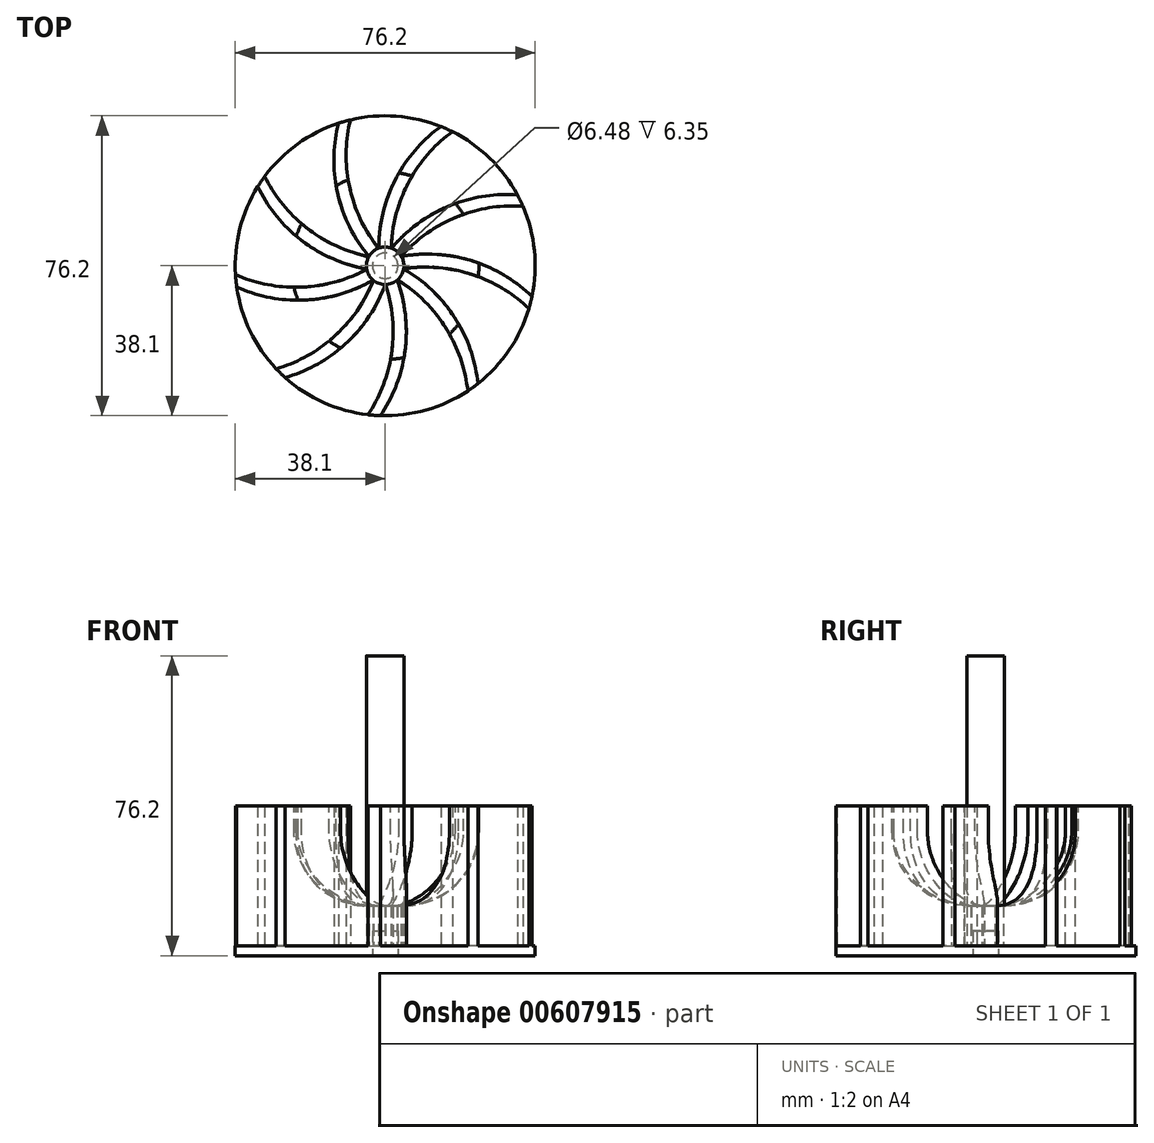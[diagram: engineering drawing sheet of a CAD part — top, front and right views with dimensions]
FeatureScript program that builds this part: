
annotation { "Feature Type Name" : "Feature", "Feature Type Description" : "" }
export const myFeature = defineFeature(function(context is Context, id is Id, definition is map)
    precondition{}
    {
        {
            var Q0;
            Q0=qCreatedBy(makeId("Top.planeOp"),FACE);
            var sketch = newSketch(context, id + "F0", { "sketchPlane" : qUnion([Q0])});
            skCircle(sketch, "E0", {"center": v(0, 0) * mm, "radius": 38.1 * mm});
            skSolve(sketch);
        }
        {
            var Q0;
            Q0=makeQuery(id+"F0.imprint","IMPRINT",FACE,{"disambiguationData":[TD([[makeQuery(id+"F0.imprint","IMPRINT",EDGE,{"derivedFrom":sQuery(id+"F0.wireOp",EDGE,"E0")}),1.0]])]});
            extrude(context, id + "F1", {"entities" : qUnion([Q0]), "depth" : 2.54 * mm, "offsetDistance" : 25.4 * mm});
        }
        {
            var Q0;
            Q0=makeQuery(id+"F1.opExtrude","CAP_FACE",FACE,{"disambiguationData":[OSD([sQuery(id+"F0.wireOp",EDGE,"E0")])],"isStart":false});
            var sketch = newSketch(context, id + "F2", { "sketchPlane" : qUnion([Q0])});
            skArc(sketch, "E1", {"start": v(0, -4.76) * mm, "mid": v(0.04, -4.76) * mm, "end": v(0.09, -4.76) * mm});
            skArc(sketch, "E2", {"start": v(-27.68, -26.18) * mm, "mid": v(-12.74, -17.8) * mm, "end": v(-3, -3.7) * mm});
            skArc(sketch, "E3", {"start": v(-25.4, -28.4) * mm, "mid": v(-9.85, -19.64) * mm, "end": v(0, -4.76) * mm});
            skLineSegment(sketch, "E4", {"start": v(-3, -3.7) * mm, "end": v(0, -4.76) * mm, "construction": true});
            skLineSegment(sketch, "E5", {"start": v(-27.68, -26.18) * mm, "end": v(-25.4, -28.4) * mm, "construction": true});
            skArc(sketch, "E6.1.0", {"start": v(-1.2, -38.08) * mm, "mid": v(5.08, -21.38) * mm, "end": v(3.06, -3.65) * mm});
            skArc(sketch, "E6.1.1", {"start": v(-4.37, -37.85) * mm, "mid": v(1.68, -21.82) * mm, "end": v(0.09, -4.76) * mm});
            skArc(sketch, "E6.2.0", {"start": v(23.56, -29.95) * mm, "mid": v(17.63, -13.11) * mm, "end": v(4.7, -0.83) * mm});
            skArc(sketch, "E6.2.1", {"start": v(20.98, -31.8) * mm, "mid": v(15.3, -15.64) * mm, "end": v(3.13, -3.6) * mm});
            skArc(sketch, "E6.3.0", {"start": v(37.3, -7.8) * mm, "mid": v(21.93, 1.29) * mm, "end": v(4.12, 2.38) * mm});
            skArc(sketch, "E6.3.1", {"start": v(36.51, -10.88) * mm, "mid": v(21.78, -2.14) * mm, "end": v(4.7, -0.74) * mm});
            skArc(sketch, "E6.4.0", {"start": v(33.58, 18) * mm, "mid": v(15.98, 15.08) * mm, "end": v(1.63, 4.48) * mm});
            skArc(sketch, "E6.4.1", {"start": v(34.96, 15.14) * mm, "mid": v(18.06, 12.36) * mm, "end": v(4.08, 2.46) * mm});
            skArc(sketch, "E6.5.0", {"start": v(14.16, 35.37) * mm, "mid": v(2.54, 21.83) * mm, "end": v(-1.63, 4.48) * mm});
            skArc(sketch, "E6.5.1", {"start": v(17.05, 34.07) * mm, "mid": v(5.89, 21.08) * mm, "end": v(1.55, 4.5) * mm});
            skArc(sketch, "E6.6.0", {"start": v(-11.9, 36.2) * mm, "mid": v(-12.08, 18.35) * mm, "end": v(-4.12, 2.38) * mm});
            skArc(sketch, "E6.6.1", {"start": v(-8.84, 37.06) * mm, "mid": v(-9.04, 19.93) * mm, "end": v(-1.71, 4.44) * mm});
            skArc(sketch, "E6.7.0", {"start": v(-32.38, 20.08) * mm, "mid": v(-21.05, 6.3) * mm, "end": v(-4.7, -0.83) * mm});
            skArc(sketch, "E6.7.1", {"start": v(-30.6, 22.7) * mm, "mid": v(-19.73, 9.46) * mm, "end": v(-4.17, 2.3) * mm});
            skArc(sketch, "E6.8.0", {"start": v(-37.71, -5.43) * mm, "mid": v(-20.17, -8.71) * mm, "end": v(-3.06, -3.65) * mm});
            skArc(sketch, "E6.8.1", {"start": v(-38.03, -2.27) * mm, "mid": v(-21.2, -5.44) * mm, "end": v(-4.67, -0.91) * mm});
            skArc(sketch, "E7.trimOffspring", {"start": v(-3.06, -3.65) * mm, "mid": v(-3.03, -3.68) * mm, "end": v(-3, -3.7) * mm});
            skArc(sketch, "E8.trimOffspring", {"start": v(-4.7, -0.83) * mm, "mid": v(-4.68, -0.87) * mm, "end": v(-4.67, -0.91) * mm});
            skArc(sketch, "E9.trimOffspring", {"start": v(3.06, -3.65) * mm, "mid": v(3.1, -3.62) * mm, "end": v(3.13, -3.6) * mm});
            skArc(sketch, "E10.trimOffspring", {"start": v(4.7, -0.83) * mm, "mid": v(4.7, -0.78) * mm, "end": v(4.7, -0.74) * mm});
            skArc(sketch, "E11.trimOffspring", {"start": v(4.12, 2.38) * mm, "mid": v(4.1, 2.42) * mm, "end": v(4.08, 2.46) * mm});
            skArc(sketch, "E12.trimOffspring", {"start": v(1.63, 4.48) * mm, "mid": v(1.59, 4.5) * mm, "end": v(1.55, 4.5) * mm});
            skArc(sketch, "E13.trimOffspring", {"start": v(-4.12, 2.38) * mm, "mid": v(-4.15, 2.34) * mm, "end": v(-4.17, 2.3) * mm});
            skArc(sketch, "E14.trimOffspring", {"start": v(-1.63, 4.48) * mm, "mid": v(-1.67, 4.46) * mm, "end": v(-1.71, 4.44) * mm});
            skCircle(sketch, "E15", {"center": v(0, 0) * mm, "radius": 38.1 * mm});
            skSolve(sketch);
        }
        {
            var Q0;
            Q0=makeQuery(id+"F2.imprint","IMPRINT",FACE,{"disambiguationData":[TD([[makeQuery(id+"F2.imprint","IMPRINT",EDGE,{"derivedFrom":sQuery(id+"F2.wireOp",EDGE,"E1")}),1.0]])]});
            extrude(context, id + "F3", {"entities" : qUnion([Q0]), "operationType" : NewBodyOperationType.ADD, "depth" : 35.56 * mm, "offsetDistance" : 25.4 * mm});
        }
        {
            var Q0;
            Q0=qCreatedBy(makeId("Front.planeOp"),FACE);
            var sketch = newSketch(context, id + "F4", { "sketchPlane" : qUnion([Q0])});
            skLineSegment(sketch, "E16", {"start": v(0, 0) * mm, "end": v(0, 35.7) * mm, "construction": true});
            skLineSegment(sketch, "E17", {"start": v(-4.76, 44.45) * mm, "end": v(-4.76, 12.7) * mm});
            skArc(sketch, "E18", {"start": v(-23.81, 31.75) * mm, "mid": v(-18.23, 18.28) * mm, "end": v(-4.76, 12.7) * mm});
            skLineSegment(sketch, "E19", {"start": v(-23.81, 31.75) * mm, "end": v(-23.81, 44.45) * mm});
            skLineSegment(sketch, "E20", {"start": v(-23.81, 44.45) * mm, "end": v(-4.76, 44.45) * mm});
            skSolve(sketch);
        }
        {
            var Q0;
            Q0=makeQuery(id+"F4.imprint","IMPRINT",FACE,{"disambiguationData":[TD([[makeQuery(id+"F4.imprint","IMPRINT",EDGE,{"derivedFrom":sQuery(id+"F4.wireOp",EDGE,"E17")}),-1.0]])]});
            var Q1;
            Q1=sQuery(id+"F4.wireOp",EDGE,"E16");
            revolve(context, id + "F5", {"operationType" : NewBodyOperationType.REMOVE, "entities" : qUnion([Q0]), "axis" : qUnion([Q1]), "revolveType" : RevolveType.FULL, "oppositeDirection" : true});
        }
        {
            var Q0;
            {var subQ0=sQuery(id+"F2.wireOp",EDGE,"E9.trimOffspring");var subQ1=sQuery(id+"F2.wireOp",EDGE,"E8.trimOffspring");var subQ2=sQuery(id+"F2.wireOp",EDGE,"E1");var subQ3=sQuery(id+"F2.wireOp",EDGE,"E7.trimOffspring");var subQ4=sQuery(id+"F2.wireOp",EDGE,"E10.trimOffspring");var subQ5=sQuery(id+"F2.wireOp",EDGE,"E11.trimOffspring");var subQ6=sQuery(id+"F2.wireOp",EDGE,"E12.trimOffspring");var subQ7=sQuery(id+"F2.wireOp",EDGE,"E13.trimOffspring");var subQ8=sQuery(id+"F2.wireOp",EDGE,"E14.trimOffspring");Q0=makeQuery(id+"F5.boolean.opBoolean","SPLIT",FACE,{"disambiguationData":[TD([makeQuery(id+"F3.opExtrude","SWEPT_FACE",FACE,{"disambiguationData":[OSD([subQ2])]})])],"derivedFrom":makeQuery(id+"F3.opExtrude","CAP_FACE",FACE,{"disambiguationData":[OSD([subQ2,sQuery(id+"F2.wireOp",EDGE,"E2"),sQuery(id+"F2.wireOp",EDGE,"E3"),sQuery(id+"F2.wireOp",EDGE,"E6.1.0"),sQuery(id+"F2.wireOp",EDGE,"E6.1.1"),sQuery(id+"F2.wireOp",EDGE,"E6.2.0"),sQuery(id+"F2.wireOp",EDGE,"E6.2.1"),sQuery(id+"F2.wireOp",EDGE,"E6.3.0"),sQuery(id+"F2.wireOp",EDGE,"E6.3.1"),sQuery(id+"F2.wireOp",EDGE,"E6.4.0"),sQuery(id+"F2.wireOp",EDGE,"E6.4.1"),sQuery(id+"F2.wireOp",EDGE,"E6.5.0"),sQuery(id+"F2.wireOp",EDGE,"E6.5.1"),sQuery(id+"F2.wireOp",EDGE,"E6.6.0"),sQuery(id+"F2.wireOp",EDGE,"E6.6.1"),sQuery(id+"F2.wireOp",EDGE,"E6.7.0"),sQuery(id+"F2.wireOp",EDGE,"E6.7.1"),sQuery(id+"F2.wireOp",EDGE,"E6.8.0"),sQuery(id+"F2.wireOp",EDGE,"E6.8.1"),subQ3,subQ1,subQ0,subQ4,subQ5,subQ6,subQ7,subQ8,sQuery(id+"F2.wireOp",EDGE,"E15")])],"isStart":false})});}
            var sketch = newSketch(context, id + "F6", { "sketchPlane" : qUnion([Q0])});
            skCircle(sketch, "E21", {"center": v(0, 0) * mm, "radius": 4.76 * mm});
            skSolve(sketch);
        }
        {
            var Q0;
            Q0=makeQuery(id+"F6.imprint","IMPRINT",FACE,{"disambiguationData":[TD([[makeQuery(id+"F6.imprint","IMPRINT",EDGE,{"derivedFrom":sQuery(id+"F6.wireOp",EDGE,"E21")}),1.0]])]});
            extrude(context, id + "F7", {"entities" : qUnion([Q0]), "operationType" : NewBodyOperationType.ADD, "depth" : 38.1 * mm, "offsetDistance" : 25.4 * mm});
        }
        {
            var Q0;
            Q0=makeQuery(id+"F1.opExtrude","CAP_FACE",FACE,{"disambiguationData":[OSD([sQuery(id+"F0.wireOp",EDGE,"E0")])],"isStart":true});
            var sketch = newSketch(context, id + "F8", { "sketchPlane" : qUnion([Q0])});
            skCircle(sketch, "E22", {"center": v(0, 0) * mm, "radius": 3.24 * mm});
            skSolve(sketch);
        }
        {
            var Q0;
            Q0 = qSketchRegion(id + "F8", true);
            extrude(context, id + "F9", {"entities" : qUnion([Q0]), "operationType" : NewBodyOperationType.REMOVE, "oppositeDirection" : true, "depth" : 6.35 * mm, "offsetDistance" : 25.4 * mm});
        }
    });
